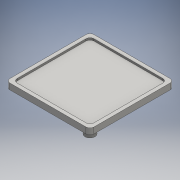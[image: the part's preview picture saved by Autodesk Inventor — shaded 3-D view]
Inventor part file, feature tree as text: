
AUTODESK INVENTOR PART (.ipt)
format: ipt  version: 2016 (Build 200138000, 138)  size: 163,328 bytes
history: native  units: mm
features: extrude x3, sketch x2, fillet x2
ambient origin geometry x8: Origin, YZ Plane, XZ Plane, XY Plane, X Axis, Y Axis, Z Axis, Center Point
bodies: Solid1 (feature_tree)
feature tree (7):
  sketch  "Sketch Base"  dims[d2=30.0mm d3=30.0mm d4=3.0mm d6=3.0mm d8=5.0mm d11=5.0mm d12=38.0mm d13=38.0mm d14=42.0mm d15=42.0mm d16=5.0mm d17=0.0mm d24=2.0mm d25=0.0mm d30=38.4mm d31=38.4mm d32=1.0mm d33=0.0mm d34=2.0mm d35=2.0mm]
  extrude  "Extrusion1"  Depth=36.0mm
  extrude  "Extrusion5"  Depth=2.0mm
  extrude  "Extrusion8"  Depth=3.0mm
  fillet  "Fillet1"  Radius=3.0mm
  fillet  "Fillet2"  Radius=5.0mm
  sketch  "Sketch2"  dims[d0=36.0mm d1=36.0mm]
